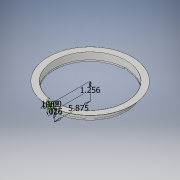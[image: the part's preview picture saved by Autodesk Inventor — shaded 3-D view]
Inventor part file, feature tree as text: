
AUTODESK INVENTOR PART (.ipt)
format: ipt  version: 2017 (Build 210142000, 142)  size: 168,960 bytes
history: native  units: in
note: dims shown in document units (in); Inventor stores cm internally (conversion verified against a paired STEP export)
features: sketch x2, revolve x1, plane x1, extrude x1
ambient origin geometry x8: Origin, YZ Plane, XZ Plane, XY Plane, X Axis, Y Axis, Z Axis, Center Point
bodies: Solid1 (feature_tree)
feature tree (5):
  revolve  "Revolution1"  [1 undecoded]
  plane  "Work Plane1"
  extrude  "Extrusion1"  Depth=0.5in
  sketch  "Sketch1"  dims[d0=1.256in d1=5.875in]
  sketch  "Sketch2"  dims[d2=1.0in d3=0.0312in d4=0.9688in d5=0.125in d6=0.0156in d8=90.0deg d10=0.5in d11=0.0in d12=0.125in d13=1.0in d14=0.0in]
note: 1 required parameter value undecoded (feature->parameter linkage not recoverable at this tier; creation-order binding heuristic only, values carry confidence <= 0.55)
